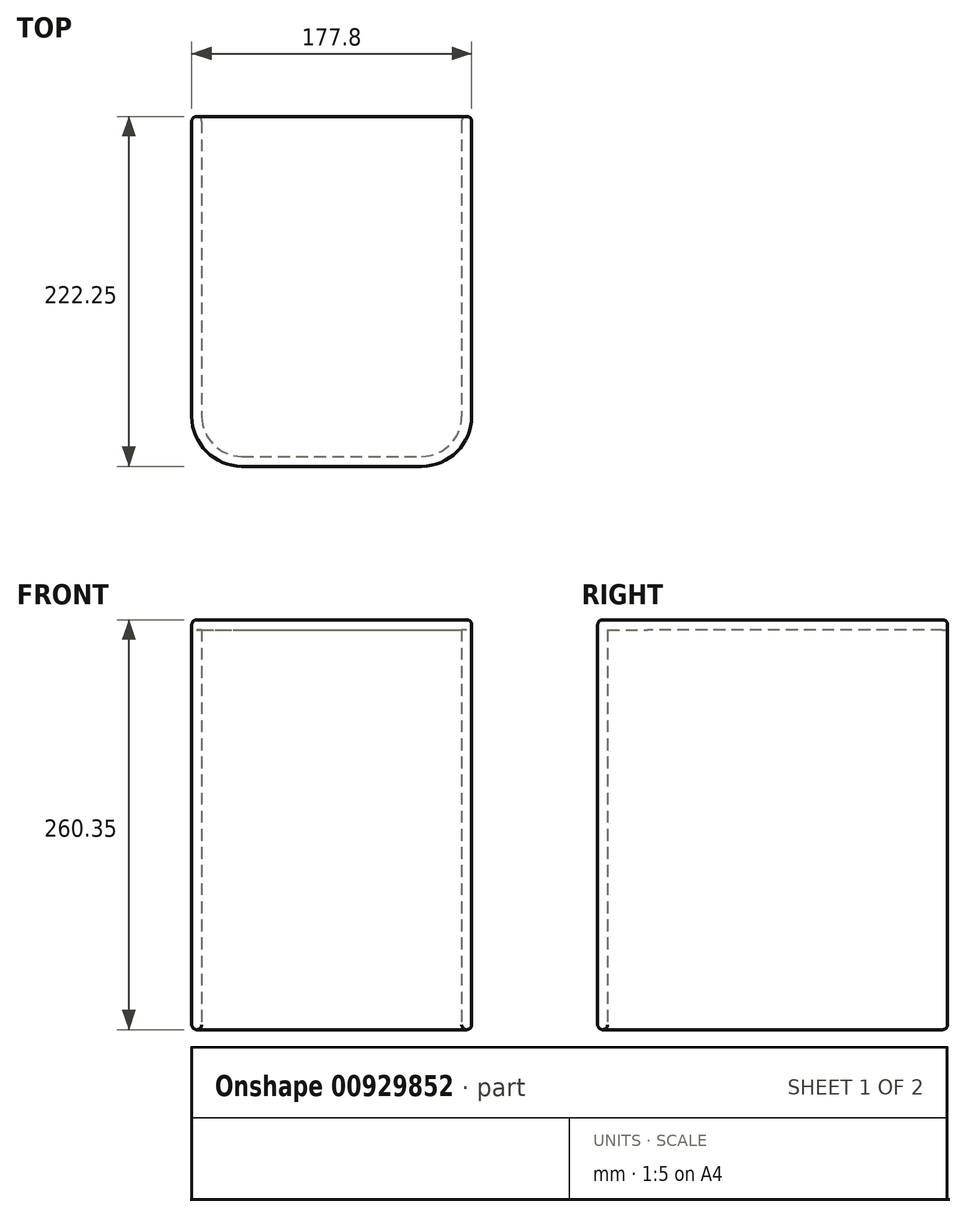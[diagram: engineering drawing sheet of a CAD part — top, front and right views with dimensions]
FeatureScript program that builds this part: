
annotation { "Feature Type Name" : "Feature", "Feature Type Description" : "" }
export const myFeature = defineFeature(function(context is Context, id is Id, definition is map)
    precondition{}
    {
        {
            var Q0;
            Q0=qCreatedBy(makeId("Top.planeOp"),FACE);
            var sketch = newSketch(context, id + "F0", { "sketchPlane" : qUnion([Q0])});
            skLineSegment(sketch, "E0.bottom", {"start": v(-82.55, 0) * mm, "end": v(82.55, 0) * mm, "construction": true});
            skLineSegment(sketch, "E0.top", {"start": v(-57.15, -215.9) * mm, "end": v(57.15, -215.9) * mm});
            skLineSegment(sketch, "E0.left", {"start": v(-82.55, 0) * mm, "end": v(-82.55, -190.5) * mm});
            skLineSegment(sketch, "E0.right", {"start": v(82.55, 0) * mm, "end": v(82.55, -190.5) * mm});
            skPoint(sketch, "E1", {"position": v(0, 0) * mm});
            skPoint(sketch, "E2.visualSharp", {"position": v(-82.55, -215.9) * mm});
            skArc(sketch, "E2.filletArc", {"start": v(-82.55, -190.5) * mm, "mid": v(-75.11, -208.46) * mm, "end": v(-57.15, -215.9) * mm});
            skPoint(sketch, "E3.visualSharp", {"position": v(82.55, -215.9) * mm});
            skArc(sketch, "E3.filletArc", {"start": v(57.15, -215.9) * mm, "mid": v(75.11, -208.46) * mm, "end": v(82.55, -190.5) * mm});
            skLineSegment(sketch, "E4.0", {"start": v(88.9, 0) * mm, "end": v(88.9, -190.5) * mm});
            skLineSegment(sketch, "E4.1", {"start": v(-88.9, 0) * mm, "end": v(-88.9, -190.5) * mm});
            skArc(sketch, "E4.2", {"start": v(-88.9, -190.5) * mm, "mid": v(-79.6, -212.95) * mm, "end": v(-57.15, -222.25) * mm});
            skLineSegment(sketch, "E4.3", {"start": v(-57.15, -222.25) * mm, "end": v(57.15, -222.25) * mm});
            skArc(sketch, "E4.4", {"start": v(57.15, -222.25) * mm, "mid": v(79.6, -212.95) * mm, "end": v(88.9, -190.5) * mm});
            skLineSegment(sketch, "E5", {"start": v(-88.9, 0) * mm, "end": v(-82.55, 0) * mm});
            skLineSegment(sketch, "E6", {"start": v(82.55, 0) * mm, "end": v(88.9, 0) * mm});
            skSolve(sketch);
        }
        {
            var Q0;
            Q0=makeQuery(id+"F0.imprint","IMPRINT",FACE,{"disambiguationData":[TD([[makeQuery(id+"F0.imprint","IMPRINT",EDGE,{"derivedFrom":sQuery(id+"F0.wireOp",EDGE,"E0.top")}),-1.0]])]});
            extrude(context, id + "F1", {"entities" : qUnion([Q0]), "depth" : 254 * mm, "offsetDistance" : 25.4 * mm});
        }
        {
            var Q0;
            Q0=makeQuery(id+"F1.opExtrude","CAP_FACE",FACE,{"disambiguationData":[OSD([sQuery(id+"F0.wireOp",EDGE,"E0.top"),sQuery(id+"F0.wireOp",EDGE,"E0.left"),sQuery(id+"F0.wireOp",EDGE,"E0.right"),sQuery(id+"F0.wireOp",EDGE,"E2.filletArc"),sQuery(id+"F0.wireOp",EDGE,"E3.filletArc"),sQuery(id+"F0.wireOp",EDGE,"E4.0"),sQuery(id+"F0.wireOp",EDGE,"E4.1"),sQuery(id+"F0.wireOp",EDGE,"E4.2"),sQuery(id+"F0.wireOp",EDGE,"E4.3"),sQuery(id+"F0.wireOp",EDGE,"E4.4"),sQuery(id+"F0.wireOp",EDGE,"E5"),sQuery(id+"F0.wireOp",EDGE,"E6")])],"isStart":false});
            var sketch = newSketch(context, id + "F2", { "sketchPlane" : qUnion([Q0])});
            skLineSegment(sketch, "E7", {"start": v(-88.9, 0) * mm, "end": v(88.9, 0) * mm});
            skSolve(sketch);
        }
        {
            var Q0;
            Q0 = qSketchRegion(id + "F2", true);
            var Q1;
            Q1=makeQuery(id+"F2.imprint","IMPRINT",FACE,{"disambiguationData":[TD([[makeQuery(id+"F2.imprint","IMPRINT",EDGE,{"derivedFrom":makeQuery(id+"F1.opExtrude","CAP_EDGE",EDGE,{"disambiguationData":[OSD([sQuery(id+"F0.wireOp",EDGE,"E0.top")])],"isStart":false})}),1.0]])]});
            var Q2;
            Q2=makeQuery(id+"F2.imprint","IMPRINT",FACE,{"disambiguationData":[TD([[makeQuery(id+"F2.imprint","IMPRINT",EDGE,{"derivedFrom":makeQuery(id+"F1.opExtrude","CAP_EDGE",EDGE,{"disambiguationData":[OSD([sQuery(id+"F0.wireOp",EDGE,"E0.top")])],"isStart":false})}),-1.0]])]});
            extrude(context, id + "F3", {"entities" : qUnion([Q0, Q1, Q2]), "operationType" : NewBodyOperationType.ADD, "depth" : 6.35 * mm, "offsetDistance" : 25.4 * mm});
        }
        {
            var Q0;
            Q0=makeQuery(id+"F1.opExtrude","CAP_EDGE",EDGE,{"disambiguationData":[OSD([sQuery(id+"F0.wireOp",EDGE,"E3.filletArc")])],"isStart":false});
            var Q1;
            Q1=makeQuery(id+"F3.opExtrude","CAP_FACE",FACE,{"disambiguationData":[OSD([sQuery(id+"F0.wireOp",EDGE,"E4.0"),sQuery(id+"F0.wireOp",EDGE,"E4.1"),sQuery(id+"F0.wireOp",EDGE,"E4.2"),sQuery(id+"F0.wireOp",EDGE,"E4.3"),sQuery(id+"F0.wireOp",EDGE,"E4.4"),sQuery(id+"F2.wireOp",EDGE,"E7")])],"isStart":false});
            var Q2;
            {var subQ0=sQuery(id+"F0.wireOp",EDGE,"E4.0");Q2=makeQuery(id+"F3.boolean.opBoolean","MERGE",EDGE,{"derivedFrom":[makeQuery(id+"F1.opExtrude","SWEPT_EDGE",EDGE,{"disambiguationData":[OSD([subQ0,sQuery(id+"F0.wireOp",EDGE,"E6")])]}),makeQuery(id+"F3.opExtrude","SWEPT_EDGE",EDGE,{"disambiguationData":[OSD([subQ0,sQuery(id+"F2.wireOp",EDGE,"E7")])]})]});}
            var Q3;
            {var subQ0=sQuery(id+"F0.wireOp",EDGE,"E4.1");Q3=makeQuery(id+"F3.boolean.opBoolean","MERGE",EDGE,{"derivedFrom":[makeQuery(id+"F1.opExtrude","SWEPT_EDGE",EDGE,{"disambiguationData":[OSD([subQ0,sQuery(id+"F0.wireOp",EDGE,"E5")])]}),makeQuery(id+"F3.opExtrude","SWEPT_EDGE",EDGE,{"disambiguationData":[OSD([subQ0,sQuery(id+"F2.wireOp",EDGE,"E7")])]})]});}
            var Q4;
            Q4=makeQuery(id+"F1.opExtrude","SWEPT_EDGE",EDGE,{"disambiguationData":[OSD([sQuery(id+"F0.wireOp",EDGE,"E0.right"),sQuery(id+"F0.wireOp",EDGE,"E6")])]});
            var Q5;
            Q5=makeQuery(id+"F1.opExtrude","SWEPT_EDGE",EDGE,{"disambiguationData":[OSD([sQuery(id+"F0.wireOp",EDGE,"E0.left"),sQuery(id+"F0.wireOp",EDGE,"E5")])]});
            var Q6;
            Q6=makeQuery(id+"F1.opExtrude","CAP_FACE",FACE,{"disambiguationData":[OSD([sQuery(id+"F0.wireOp",EDGE,"E0.top"),sQuery(id+"F0.wireOp",EDGE,"E0.left"),sQuery(id+"F0.wireOp",EDGE,"E0.right"),sQuery(id+"F0.wireOp",EDGE,"E2.filletArc"),sQuery(id+"F0.wireOp",EDGE,"E3.filletArc"),sQuery(id+"F0.wireOp",EDGE,"E4.0"),sQuery(id+"F0.wireOp",EDGE,"E4.1"),sQuery(id+"F0.wireOp",EDGE,"E4.2"),sQuery(id+"F0.wireOp",EDGE,"E4.3"),sQuery(id+"F0.wireOp",EDGE,"E4.4"),sQuery(id+"F0.wireOp",EDGE,"E5"),sQuery(id+"F0.wireOp",EDGE,"E6")])],"isStart":true});
            fillet(context, id + "F4", {"entities" : qUnion([Q0, Q1, Q2, Q3, Q4, Q5, Q6]), "radius" : 3.17 * mm, "tangentPropagation" : true, "allowEdgeOverflow" : false});
        }
    });
